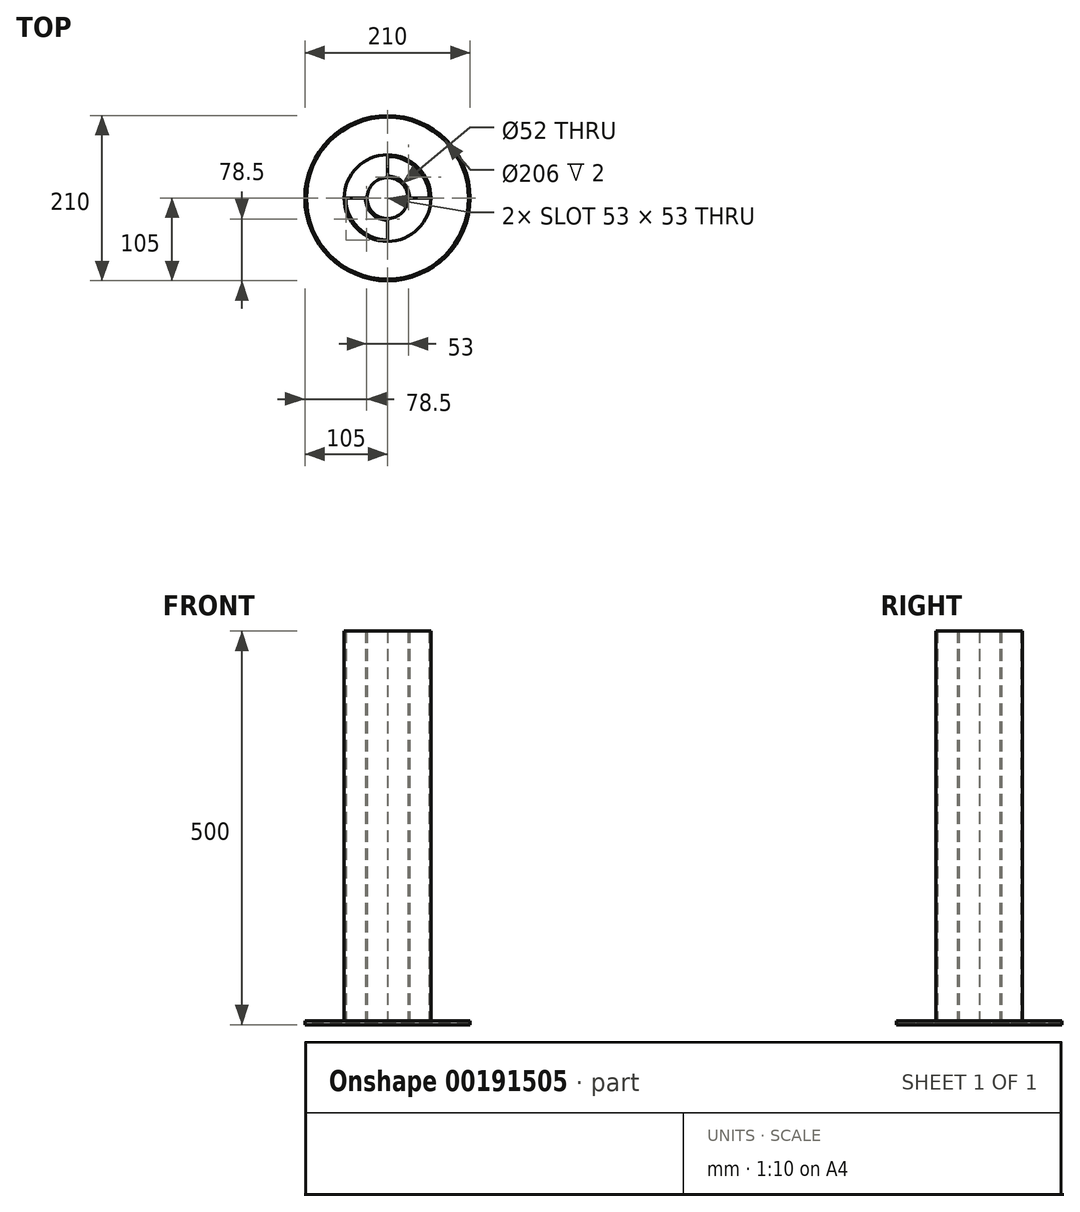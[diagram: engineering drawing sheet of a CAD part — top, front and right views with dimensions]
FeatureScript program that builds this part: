
annotation { "Feature Type Name" : "Feature", "Feature Type Description" : "" }
export const myFeature = defineFeature(function(context is Context, id is Id, definition is map)
    precondition{}
    {
        {
            var Q0;
            Q0=qCreatedBy(makeId("Top.planeOp"),FACE);
            var sketch = newSketch(context, id + "F0", { "sketchPlane" : qUnion([Q0])});
            skCircle(sketch, "E0", {"center": v(0, 0) * mm, "radius": 105 * mm});
            skCircle(sketch, "E1", {"center": v(0, 0) * mm, "radius": 26 * mm});
            skCircle(sketch, "E2", {"center": v(0, 0) * mm, "radius": 28 * mm});
            skCircle(sketch, "E3", {"center": v(0, 0) * mm, "radius": 55 * mm});
            skCircle(sketch, "E4", {"center": v(0, 0) * mm, "radius": 53 * mm});
            skLineSegment(sketch, "E5", {"start": v(0, 53) * mm, "end": v(0, 28) * mm});
            skLineSegment(sketch, "E6", {"start": v(28, 0) * mm, "end": v(53, 0) * mm});
            skLineSegment(sketch, "E7", {"start": v(0, -28) * mm, "end": v(0, -53) * mm});
            skLineSegment(sketch, "E8", {"start": v(-28, 0) * mm, "end": v(-53, 0) * mm});
            skSolve(sketch);
        }
        {
            var Q0;
            Q0 = qSketchRegion(id + "F0", true);
            var Q1;
            Q1=makeQuery(id+"F0.imprint","IMPRINT",FACE,{"disambiguationData":[TD([[makeQuery(id+"F0.imprint","IMPRINT",EDGE,{"derivedFrom":sQuery(id+"F0.wireOp",EDGE,"E3")}),1.0]])]});
            var Q2;
            Q2=makeQuery(id+"F0.imprint","IMPRINT",FACE,{"disambiguationData":[TD([[makeQuery(id+"F0.imprint","IMPRINT",EDGE,{"derivedFrom":sQuery(id+"F0.wireOp",EDGE,"E2")}),-1.0]])]});
            var Q3;
            Q3=makeQuery(id+"F0.imprint","IMPRINT",FACE,{"disambiguationData":[TD([[makeQuery(id+"F0.imprint","IMPRINT",EDGE,{"derivedFrom":sQuery(id+"F0.wireOp",EDGE,"E1")}),-1.0]])]});
            extrude(context, id + "F1", {"entities" : qUnion([Q0, Q1, Q2, Q3]), "depth" : 3 * mm});
        }
        {
            var Q0;
            Q0=makeQuery(id+"F0.imprint","IMPRINT",FACE,{"disambiguationData":[TD([[makeQuery(id+"F0.imprint","IMPRINT",EDGE,{"derivedFrom":sQuery(id+"F0.wireOp",EDGE,"E1")}),-1.0]])]});
            extrude(context, id + "F2", {"entities" : qUnion([Q0]), "operationType" : NewBodyOperationType.ADD, "depth" : 500 * mm});
        }
        {
            var Q0;
            Q0=makeQuery(id+"F0.imprint","IMPRINT",FACE,{"disambiguationData":[TD([[makeQuery(id+"F0.imprint","IMPRINT",EDGE,{"derivedFrom":sQuery(id+"F0.wireOp",EDGE,"E3")}),1.0]])]});
            extrude(context, id + "F3", {"entities" : qUnion([Q0]), "operationType" : NewBodyOperationType.ADD, "depth" : 500 * mm});
        }
        {
            var Q0;
            {var subQ0=sQuery(id+"F0.wireOp",EDGE,"E0");Q0=makeQuery(id+"F3.boolean.opBoolean","SPLIT",FACE,{"disambiguationData":[TD([makeQuery(id+"F1.opExtrude","SWEPT_FACE",FACE,{"disambiguationData":[OSD([subQ0])]})])],"derivedFrom":makeQuery(id+"F1.opExtrude","CAP_FACE",FACE,{"disambiguationData":[OSD([subQ0,sQuery(id+"F0.wireOp",EDGE,"E1")])],"isStart":false})});}
            var sketch = newSketch(context, id + "F4", { "sketchPlane" : qUnion([Q0])});
            skCircle(sketch, "E9", {"center": v(0, 0) * mm, "radius": 105 * mm});
            skCircle(sketch, "E10", {"center": v(0, 0) * mm, "radius": 103 * mm});
            skSolve(sketch);
        }
        {
            var Q0;
            Q0 = qSketchRegion(id + "F4", true);
            extrude(context, id + "F5", {"entities" : qUnion([Q0]), "operationType" : NewBodyOperationType.ADD, "depth" : 2 * mm});
        }
        {
            var Q0;
            {var subQ0=sQuery(id+"F0.wireOp",EDGE,"E5");Q0=makeQuery(id+"F0.imprint","IMPRINT",FACE,{"disambiguationData":[TD([[makeQuery(id+"F0.imprint","IMPRINT",EDGE,{"derivedFrom":subQ0}),-1.0]])]});}
            var Q1;
            {var subQ0=sQuery(id+"F0.wireOp",EDGE,"E6");Q1=makeQuery(id+"F0.imprint","IMPRINT",FACE,{"disambiguationData":[TD([[makeQuery(id+"F0.imprint","IMPRINT",EDGE,{"derivedFrom":subQ0}),-1.0]])]});}
            extrude(context, id + "F6", {"entities" : qUnion([Q0, Q1]), "operationType" : NewBodyOperationType.ADD, "depth" : 500 * mm});
        }
        {
            var Q0;
            {var subQ0=sQuery(id+"F0.wireOp",EDGE,"E7");Q0=makeQuery(id+"F0.imprint","IMPRINT",FACE,{"disambiguationData":[TD([[makeQuery(id+"F0.imprint","IMPRINT",EDGE,{"derivedFrom":subQ0}),-1.0]])]});}
            var Q1;
            {var subQ0=sQuery(id+"F0.wireOp",EDGE,"E5");Q1=makeQuery(id+"F0.imprint","IMPRINT",FACE,{"disambiguationData":[TD([[makeQuery(id+"F0.imprint","IMPRINT",EDGE,{"derivedFrom":subQ0}),1.0]])]});}
            extrude(context, id + "F7", {"entities" : qUnion([Q0, Q1]), "operationType" : NewBodyOperationType.REMOVE, "depth" : 25 * mm});
        }
    });
